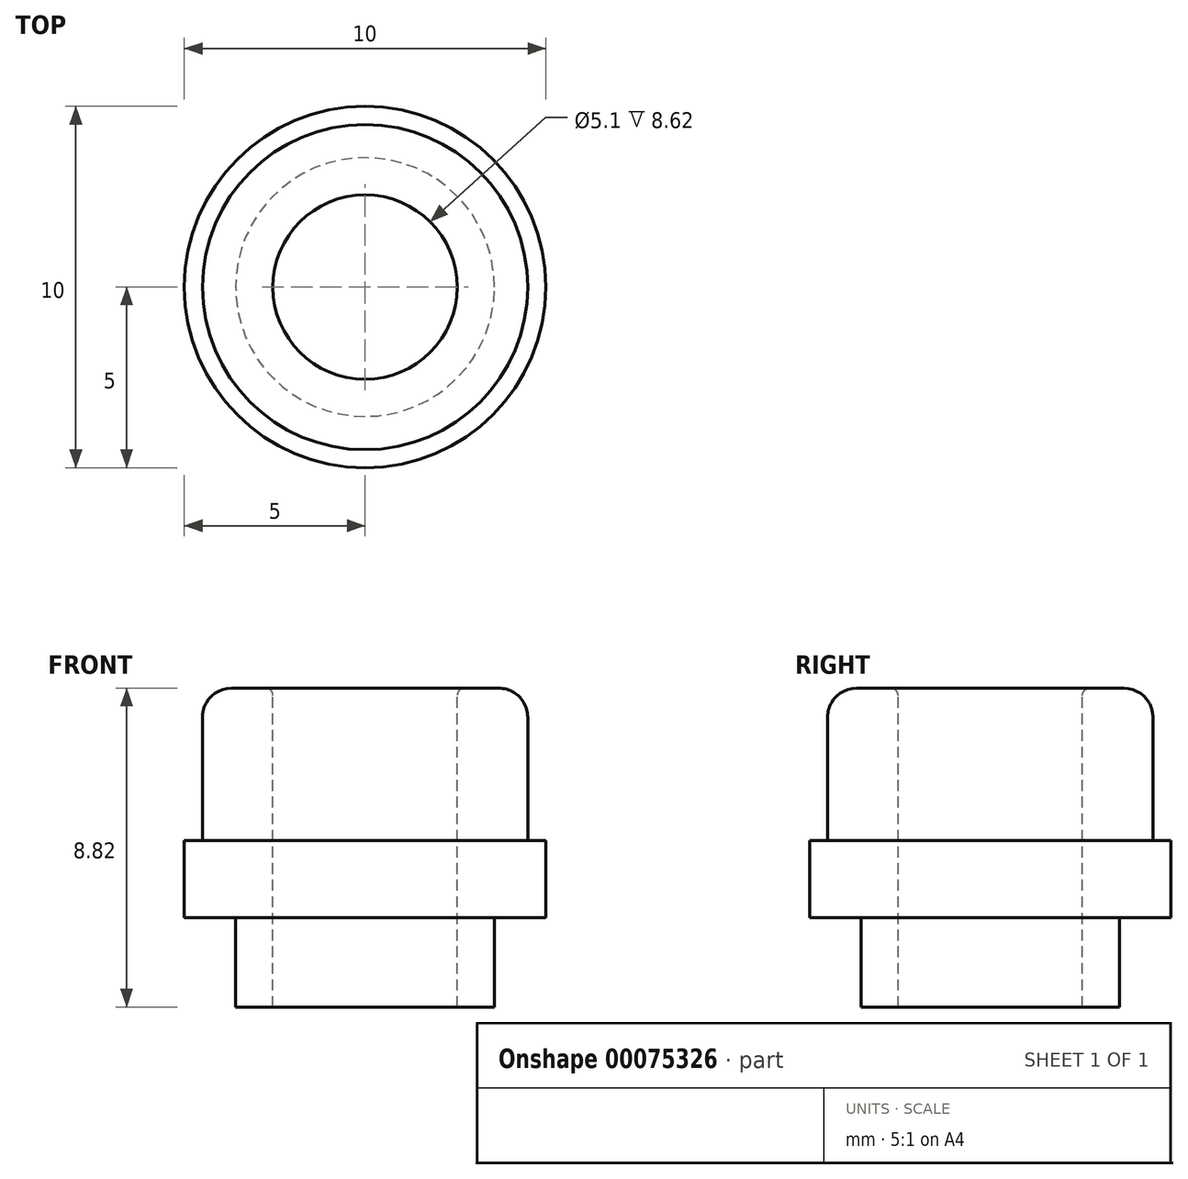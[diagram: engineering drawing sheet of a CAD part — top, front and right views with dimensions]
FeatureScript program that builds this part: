
annotation { "Feature Type Name" : "Feature", "Feature Type Description" : "" }
export const myFeature = defineFeature(function(context is Context, id is Id, definition is map)
    precondition{}
    {
        {
            var Q0;
            Q0=qCreatedBy(makeId("Front.planeOp"),FACE);
            var sketch = newSketch(context, id + "F0", { "sketchPlane" : qUnion([Q0])});
            skLineSegment(sketch, "E0", {"start": v(0, 5.54) * mm, "end": v(0, -7.32) * mm, "construction": true});
            skLineSegment(sketch, "E1", {"start": v(-2.55, 6.35) * mm, "end": v(-4.5, 6.35) * mm});
            skLineSegment(sketch, "E2", {"start": v(-4.5, 6.35) * mm, "end": v(-4.5, 2.13) * mm});
            skLineSegment(sketch, "E3", {"start": v(-4.5, 2.13) * mm, "end": v(-5, 2.13) * mm});
            skLineSegment(sketch, "E4", {"start": v(-5, 2.13) * mm, "end": v(-5, 0) * mm});
            skLineSegment(sketch, "E5", {"start": v(-5, 0) * mm, "end": v(-3.58, 0) * mm});
            skLineSegment(sketch, "E6", {"start": v(-3.58, 0) * mm, "end": v(-3.58, -2.47) * mm});
            skLineSegment(sketch, "E7", {"start": v(-3.58, -2.47) * mm, "end": v(-2.55, -2.47) * mm});
            skLineSegment(sketch, "E8", {"start": v(-2.55, -2.47) * mm, "end": v(-2.55, 6.35) * mm});
            skSolve(sketch);
        }
        {
            var Q0;
            Q0=qSketchRegion(id+"F0",true);
            var Q1;
            Q1=sQuery(id+"F0.wireOp",EDGE,"E0");
            revolve(context, id + "F1", {"entities" : qUnion([Q0]), "axis" : qUnion([Q1]), "revolveType" : RevolveType.FULL});
        }
        {
            var Q0;
            Q0=makeQuery(id+"F1.opRevolve","SWEPT_EDGE",EDGE,{"disambiguationData":[OSD([sQuery(id+"F0.wireOp",EDGE,"E1"),sQuery(id+"F0.wireOp",EDGE,"E2")])]});
            fillet(context, id + "F2", {"entities" : qUnion([Q0]), "radius" : 0.8 * mm, "tangentPropagation" : true, "allowEdgeOverflow" : false});
        }
        {
            var Q0;
            Q0=makeQuery(id+"F1.opRevolve","SWEPT_EDGE",EDGE,{"disambiguationData":[OSD([sQuery(id+"F0.wireOp",EDGE,"E1"),sQuery(id+"F0.wireOp",EDGE,"E8")])]});
            fillet(context, id + "F3", {"entities" : qUnion([Q0]), "radius" : 0.2 * mm, "tangentPropagation" : true, "allowEdgeOverflow" : false});
        }
    });
